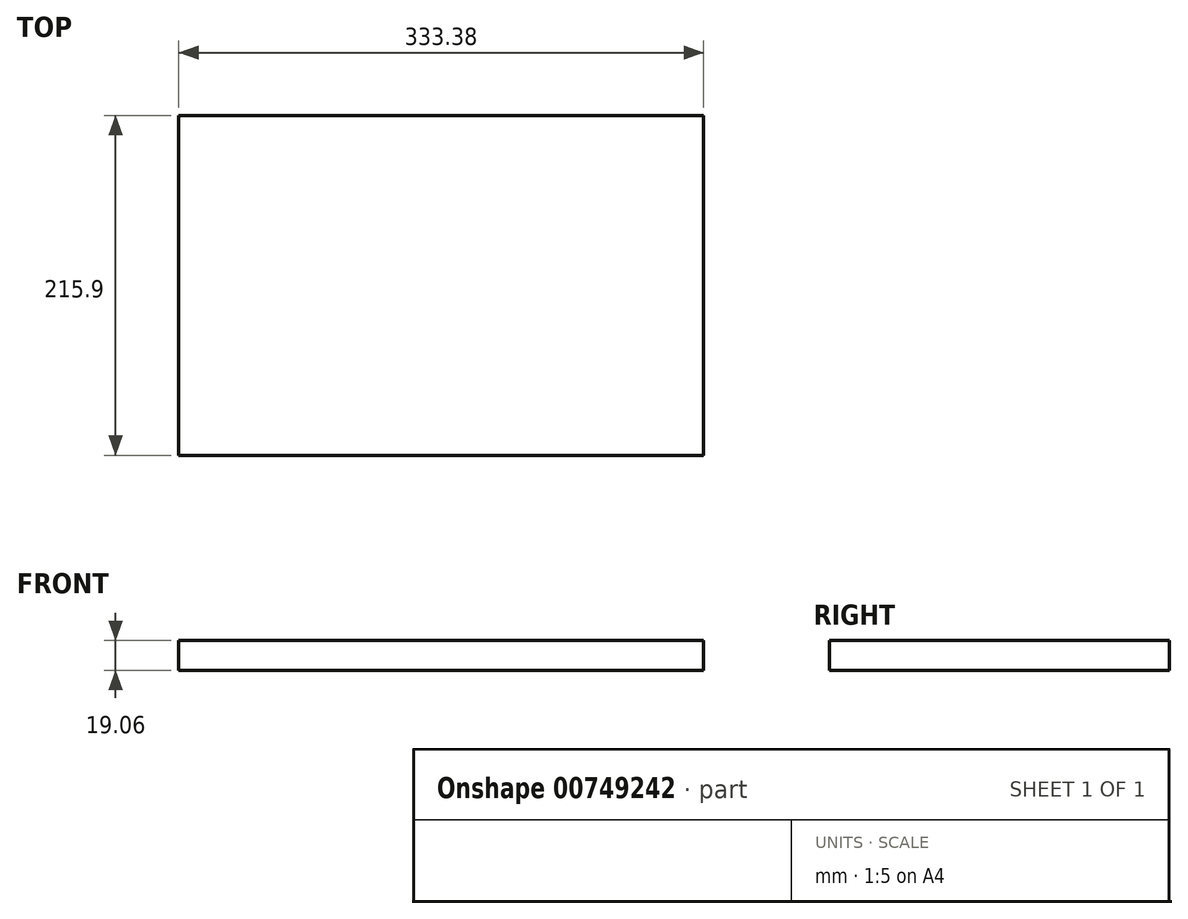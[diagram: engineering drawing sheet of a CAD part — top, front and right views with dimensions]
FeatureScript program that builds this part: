
annotation { "Feature Type Name" : "Feature", "Feature Type Description" : "" }
export const myFeature = defineFeature(function(context is Context, id is Id, definition is map)
    precondition{}
    {
        {
            var Q0;
            Q0=qCreatedBy(makeId("Right.planeOp"),FACE);
            var sketch = newSketch(context, id + "F0", { "sketchPlane" : qUnion([Q0])});
            skLineSegment(sketch, "E0.bottom", {"start": v(107.95, 9.53) * mm, "end": v(-107.95, 9.53) * mm});
            skLineSegment(sketch, "E0.top", {"start": v(107.95, -9.53) * mm, "end": v(-107.95, -9.53) * mm});
            skLineSegment(sketch, "E0.left", {"start": v(107.95, 9.53) * mm, "end": v(107.95, -9.52) * mm});
            skLineSegment(sketch, "E0.right", {"start": v(-107.95, 9.53) * mm, "end": v(-107.95, -9.52) * mm});
            skPoint(sketch, "E0.middle", {"position": v(0, 0) * mm});
            skSolve(sketch);
        }
        {
            var Q0;
            Q0 = qSketchRegion(id + "F0", true);
            extrude(context, id + "F1", {"entities" : qUnion([Q0]), "depth" : 333.38 * mm, "offsetDistance" : 25.4 * mm});
        }
    });
